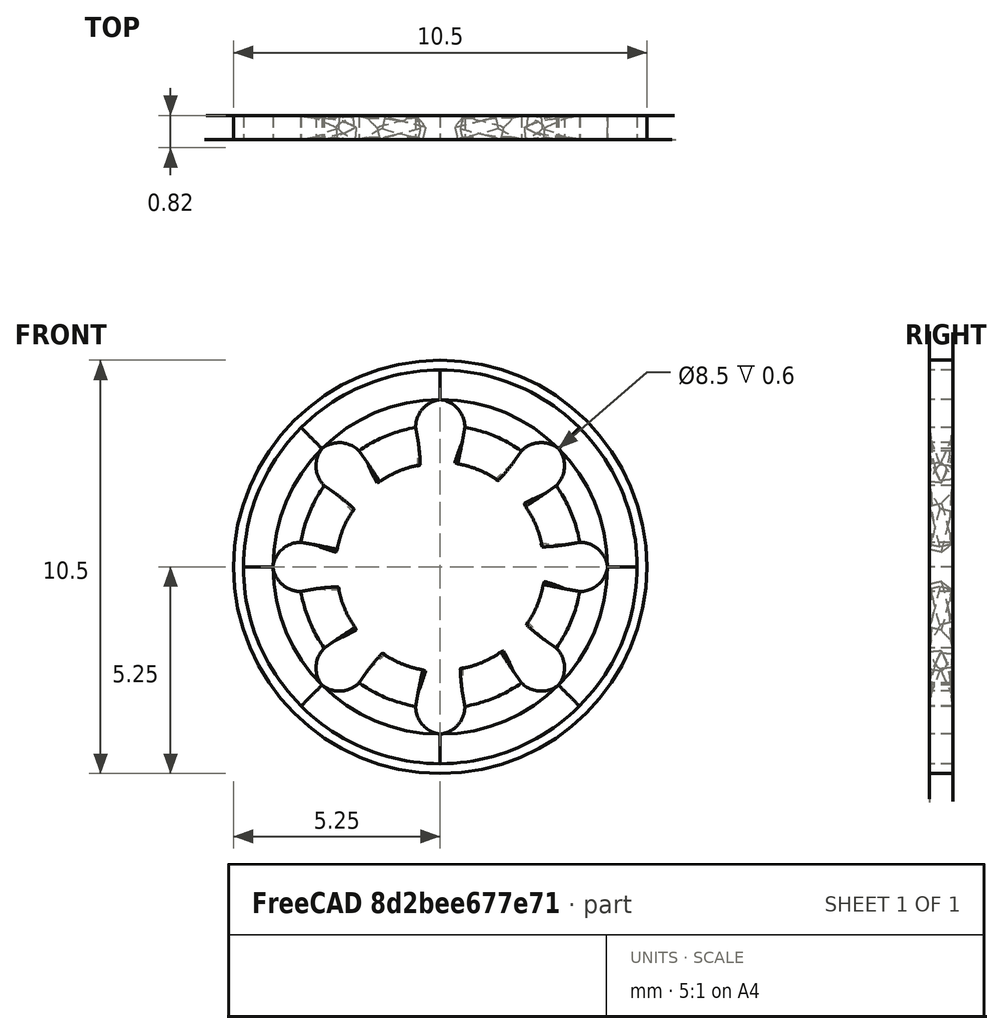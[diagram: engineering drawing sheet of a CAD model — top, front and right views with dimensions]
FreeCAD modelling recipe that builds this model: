
FCSTD DOCUMENT  (FreeCAD 0.19R24267 +99 (Git))
Label: Assembly TR Fastenings Ltd-M5 Internal Toothed Washer DIN 6797J
License: All rights reserved
LicenseURL: http://en.wikipedia.org/wiki/All_rights_reserved
objects: Part::Feature×1, Sketcher::SketchObject×1, PartDesign::Pad×1, PartDesign::Body×1
note: 5 computed .brp shape members not serialized (recipe doc carries the construction recipe); baked Part::Feature solids carry a one-line shape summary decoded from their .brp

FEATURE [Part::Feature] Part__Feature  label="TR Fastenings Ltd-M5"
  shape: bbox 12.82 x 1.154 x 12.82 mm, 104 faces, 8 solids (baked)
FEATURE [Sketcher::SketchObject] Sketch
  FullyConstrained = true
  MapMode = 5
  Placement = pos=(0,0,0) rot=(1,0,0;1.5708rad)
  Support = -> [XZ_Plane]
  sketch-geometry (2):
    g0: Circle CenterX=0 CenterY=0 CenterZ=0 NormalX=0 NormalY=0 NormalZ=1 AngleXU=0 Radius=5.25
    g1: Circle CenterX=0 CenterY=0 CenterZ=0 NormalX=0 NormalY=0 NormalZ=1 AngleXU=0 Radius=4.25
  constraints (4):
    c: Coincident(g0,g-1)
    c: Coincident(g1,g0)
    c: Diameter(g1) = 8.5
    c: Diameter(g0) = 10.5
FEATURE [PartDesign::Pad] Pad
  Direction = (1,1,1)
  Length = 0.6
  Length2 = 100
  Placement = pos=(0,0,0) rot=(1,0,0;1.5708rad)
  Profile = -> Sketch
  Reversed = true
  Type = 0
FEATURE [PartDesign::Body] Body
  Group = -> [Sketch,Pad]
  Origin = -> Origin
  Tip = -> Pad
